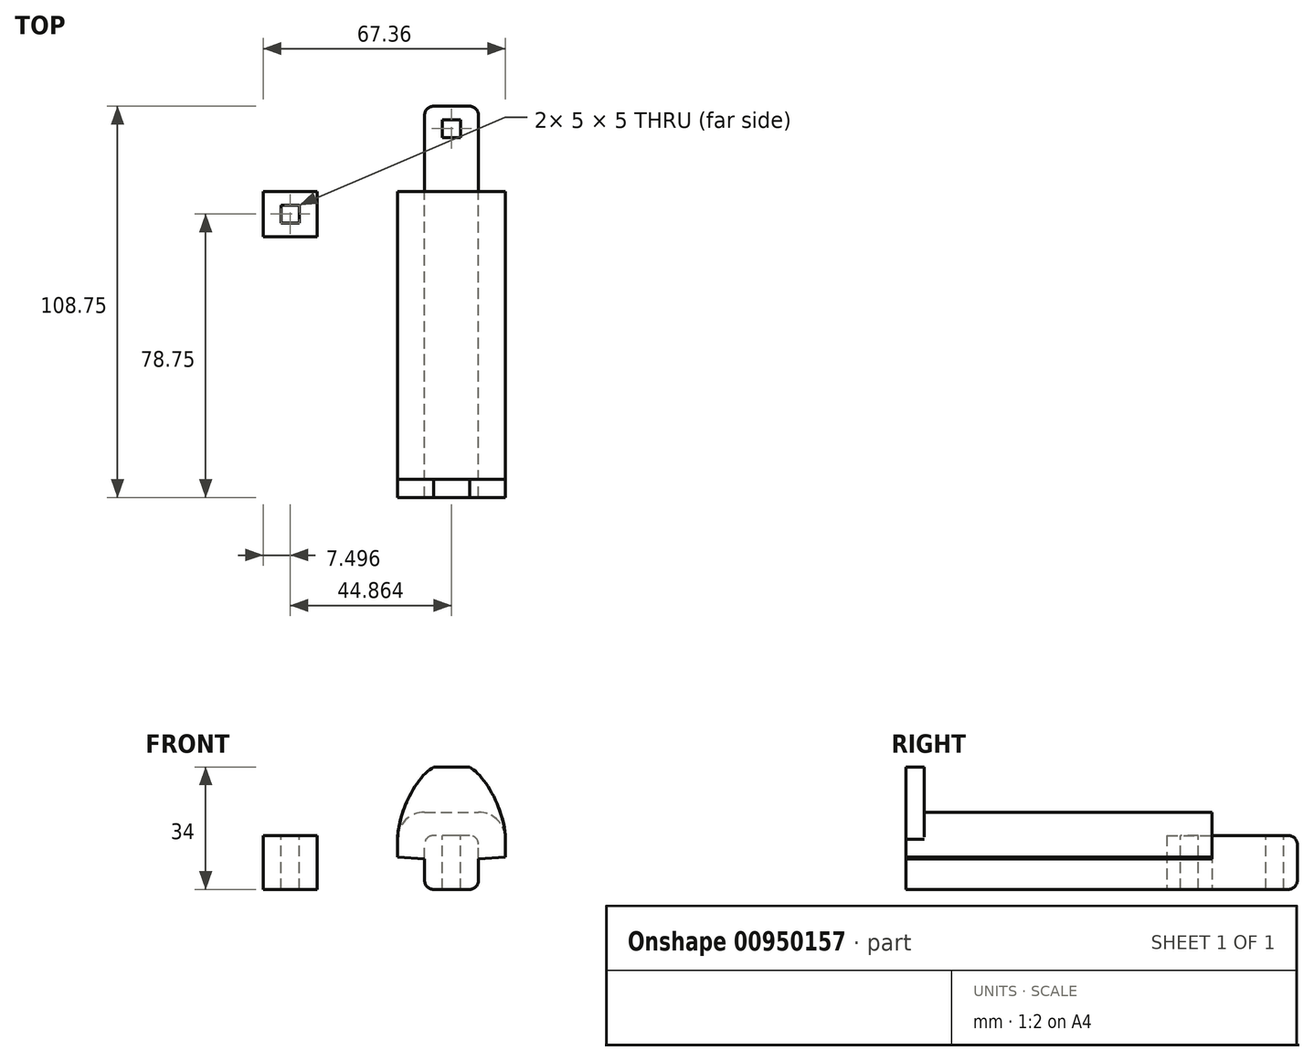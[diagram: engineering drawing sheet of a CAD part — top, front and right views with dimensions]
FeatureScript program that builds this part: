
annotation { "Feature Type Name" : "Feature", "Feature Type Description" : "" }
export const myFeature = defineFeature(function(context is Context, id is Id, definition is map)
    precondition{}
    {
        {
            var Q0;
            Q0=qCreatedBy(makeId("Front.planeOp"),FACE);
            var sketch = newSketch(context, id + "F0", { "sketchPlane" : qUnion([Q0])});
            skLineSegment(sketch, "E0.top", {"start": v(-5, -7.5) * mm, "end": v(5, -7.5) * mm});
            skPoint(sketch, "E0.middle", {"position": v(0, 0) * mm});
            skLineSegment(sketch, "E1", {"start": v(-15, 1.5) * mm, "end": v(-15, 6.5) * mm});
            skLineSegment(sketch, "E2.MirrorCS", {"start": v(15, 1.5) * mm, "end": v(15, 6.5) * mm});
            skPoint(sketch, "E3", {"position": v(7.5, 1) * mm});
            skLineSegment(sketch, "E4", {"start": v(-7.5, -5) * mm, "end": v(-7.5, 1) * mm});
            skLineSegment(sketch, "E5", {"start": v(7.5, -5) * mm, "end": v(7.5, 1) * mm});
            skLineSegment(sketch, "E6", {"start": v(-7.5, 14) * mm, "end": v(7.5, 14) * mm});
            skLineSegment(sketch, "E7", {"start": v(-7.5, 1) * mm, "end": v(-15, 1.5) * mm});
            skLineSegment(sketch, "E8", {"start": v(7.5, 1) * mm, "end": v(15, 1.5) * mm});
            skPoint(sketch, "E9.visualSharp", {"position": v(-15, 14) * mm});
            skArc(sketch, "E9.filletArc", {"start": v(-7.5, 14) * mm, "mid": v(-12.8, 11.8) * mm, "end": v(-15, 6.5) * mm});
            skPoint(sketch, "E10.visualSharp", {"position": v(15, 14) * mm});
            skArc(sketch, "E10.filletArc", {"start": v(15, 6.5) * mm, "mid": v(12.8, 11.8) * mm, "end": v(7.5, 14) * mm});
            skPoint(sketch, "E11.visualSharp", {"position": v(-7.5, -7.5) * mm});
            skArc(sketch, "E11.filletArc", {"start": v(-7.5, -5) * mm, "mid": v(-6.77, -6.77) * mm, "end": v(-5, -7.5) * mm});
            skPoint(sketch, "E12.visualSharp", {"position": v(7.5, -7.5) * mm});
            skArc(sketch, "E12.filletArc", {"start": v(5, -7.5) * mm, "mid": v(6.77, -6.77) * mm, "end": v(7.5, -5) * mm});
            skSolve(sketch);
        }
        {
            var Q0;
            Q0 = qSketchRegion(id + "F0", true);
            extrude(context, id + "F1", {"entities" : qUnion([Q0]), "depth" : 80 * mm, "offsetDistance" : 25 * mm});
        }
        {
            var Q0;
            Q0=makeQuery(id+"F1.opExtrude","CAP_FACE",FACE,{"disambiguationData":[OSD([sQuery(id+"F0.wireOp",EDGE,"E0.top"),sQuery(id+"F0.wireOp",EDGE,"E1"),sQuery(id+"F0.wireOp",EDGE,"E2.MirrorCS"),sQuery(id+"F0.wireOp",EDGE,"E4"),sQuery(id+"F0.wireOp",EDGE,"E5"),sQuery(id+"F0.wireOp",EDGE,"E6"),sQuery(id+"F0.wireOp",EDGE,"E7"),sQuery(id+"F0.wireOp",EDGE,"E8"),sQuery(id+"F0.wireOp",EDGE,"E9.filletArc"),sQuery(id+"F0.wireOp",EDGE,"E10.filletArc"),sQuery(id+"F0.wireOp",EDGE,"E11.filletArc"),sQuery(id+"F0.wireOp",EDGE,"E12.filletArc")])],"isStart":true});
            var sketch = newSketch(context, id + "F2", { "sketchPlane" : qUnion([Q0])});
            skLineSegment(sketch, "E13.bottom", {"start": v(-5, -7.5) * mm, "end": v(5, -7.5) * mm});
            skLineSegment(sketch, "E13.top", {"start": v(-5, 7.5) * mm, "end": v(5, 7.5) * mm});
            skLineSegment(sketch, "E13.left", {"start": v(-7.5, -5) * mm, "end": v(-7.5, 5) * mm});
            skLineSegment(sketch, "E13.right", {"start": v(7.5, -5) * mm, "end": v(7.5, 5) * mm});
            skPoint(sketch, "E13.middle", {"position": v(0, 0) * mm});
            skPoint(sketch, "E14.visualSharp", {"position": v(-7.5, 7.5) * mm});
            skArc(sketch, "E14.filletArc", {"start": v(-5, 7.5) * mm, "mid": v(-6.77, 6.77) * mm, "end": v(-7.5, 5) * mm});
            skPoint(sketch, "E15.visualSharp", {"position": v(7.5, 7.5) * mm});
            skArc(sketch, "E15.filletArc", {"start": v(7.5, 5) * mm, "mid": v(6.77, 6.77) * mm, "end": v(5, 7.5) * mm});
            skPoint(sketch, "E16.visualSharp", {"position": v(7.5, -7.5) * mm});
            skArc(sketch, "E16.filletArc", {"start": v(5, -7.5) * mm, "mid": v(6.77, -6.77) * mm, "end": v(7.5, -5) * mm});
            skPoint(sketch, "E17.visualSharp", {"position": v(-7.5, -7.5) * mm});
            skArc(sketch, "E17.filletArc", {"start": v(-7.5, -5) * mm, "mid": v(-6.77, -6.77) * mm, "end": v(-5, -7.5) * mm});
            skSolve(sketch);
        }
        {
            var Q0;
            Q0=makeQuery(id+"F2.imprint","IMPRINT",FACE,{"disambiguationData":[TD([[makeQuery(id+"F2.imprint","IMPRINT",EDGE,{"derivedFrom":sQuery(id+"F2.wireOp",EDGE,"E13.bottom")}),-1.0]])]});
            extrude(context, id + "F3", {"entities" : qUnion([Q0]), "operationType" : NewBodyOperationType.ADD, "depth" : 23.75 * mm, "offsetDistance" : 25 * mm});
        }
        {
            var Q0;
            Q0=makeQuery(id+"F3.opExtrude","SWEPT_FACE",FACE,{"disambiguationData":[OSD([sQuery(id+"F2.wireOp",EDGE,"E13.top")])]});
            var sketch = newSketch(context, id + "F4", { "sketchPlane" : qUnion([Q0])});
            skLineSegment(sketch, "E18.bottom", {"start": v(2.5, 20) * mm, "end": v(-2.5, 20) * mm});
            skLineSegment(sketch, "E18.top", {"start": v(2.5, 15) * mm, "end": v(-2.5, 15) * mm});
            skLineSegment(sketch, "E18.left", {"start": v(2.5, 20) * mm, "end": v(2.5, 15) * mm});
            skLineSegment(sketch, "E18.right", {"start": v(-2.5, 20) * mm, "end": v(-2.5, 15) * mm});
            skPoint(sketch, "E18.middle", {"position": v(0, 17.5) * mm});
            skSolve(sketch);
        }
        {
            var Q0;
            Q0=makeQuery(id+"F4.imprint","IMPRINT",FACE,{"disambiguationData":[TD([[makeQuery(id+"F4.imprint","IMPRINT",EDGE,{"derivedFrom":sQuery(id+"F4.wireOp",EDGE,"E18.bottom")}),1.0]])]});
            extrude(context, id + "F5", {"entities" : qUnion([Q0]), "operationType" : NewBodyOperationType.REMOVE, "oppositeDirection" : true, "depth" : 15 * mm, "offsetDistance" : 25 * mm});
        }
        {
            var Q0;
            Q0=makeQuery(id+"F1.opExtrude","CAP_FACE",FACE,{"disambiguationData":[OSD([sQuery(id+"F0.wireOp",EDGE,"E0.top"),sQuery(id+"F0.wireOp",EDGE,"E1"),sQuery(id+"F0.wireOp",EDGE,"E2.MirrorCS"),sQuery(id+"F0.wireOp",EDGE,"E4"),sQuery(id+"F0.wireOp",EDGE,"E5"),sQuery(id+"F0.wireOp",EDGE,"E6"),sQuery(id+"F0.wireOp",EDGE,"E7"),sQuery(id+"F0.wireOp",EDGE,"E8"),sQuery(id+"F0.wireOp",EDGE,"E9.filletArc"),sQuery(id+"F0.wireOp",EDGE,"E10.filletArc"),sQuery(id+"F0.wireOp",EDGE,"E11.filletArc"),sQuery(id+"F0.wireOp",EDGE,"E12.filletArc")])],"isStart":false});
            var sketch = newSketch(context, id + "F6", { "sketchPlane" : qUnion([Q0])});
            skLineSegment(sketch, "E19.top", {"start": v(-5, 26.5) * mm, "end": v(5, 26.5) * mm});
            skFitSpline(sketch, "E20", {"points": [v(-5, 26.5) * mm, v(-15, 6.5) * mm], "startDerivative": vector(-12.32, -6.2) * mm, "endDerivative": vector(-0.54, -24.82) * mm});
            skFitSpline(sketch, "E21.MirrorCS", {"points": [v(5, 26.5) * mm, v(15, 6.5) * mm], "startDerivative": vector(12.32, -6.2) * mm, "endDerivative": vector(0.54, -24.82) * mm});
            skSolve(sketch);
        }
        {
            var Q0;
            Q0=makeQuery(id+"F6.imprint","IMPRINT",FACE,{"disambiguationData":[TD([[makeQuery(id+"F6.imprint","IMPRINT",EDGE,{"derivedFrom":makeQuery(id+"F1.opExtrude","CAP_EDGE",EDGE,{"disambiguationData":[OSD([sQuery(id+"F0.wireOp",EDGE,"E0.top")])],"isStart":false})}),1.0]])]});
            var Q1;
            {var subQ1=sQuery(id+"F6.wireOp",EDGE,"E19.top");Q1=makeQuery(id+"F6.imprint","IMPRINT",FACE,{"disambiguationData":[TD([[makeQuery(id+"F6.imprint","IMPRINT",EDGE,{"derivedFrom":subQ1}),-1.0]])]});}
            extrude(context, id + "F7", {"entities" : qUnion([Q0, Q1]), "operationType" : NewBodyOperationType.ADD, "depth" : 5 * mm, "offsetDistance" : 25 * mm});
        }
        {
            var Q0;
            Q0=qCreatedBy(makeId("Front.planeOp"),FACE);
            var sketch = newSketch(context, id + "F8", { "sketchPlane" : qUnion([Q0])});
            skLineSegment(sketch, "E22.bottom", {"start": v(-52.36, 7.5) * mm, "end": v(-37.36, 7.5) * mm});
            skLineSegment(sketch, "E22.top", {"start": v(-52.36, -7.5) * mm, "end": v(-37.36, -7.5) * mm});
            skLineSegment(sketch, "E22.left", {"start": v(-52.36, 7.5) * mm, "end": v(-52.36, -7.5) * mm});
            skLineSegment(sketch, "E22.right", {"start": v(-37.36, 7.5) * mm, "end": v(-37.36, -7.5) * mm});
            skPoint(sketch, "E22.middle", {"position": v(-44.86, 0) * mm});
            skSolve(sketch);
        }
        {
            var Q0;
            Q0=makeQuery(id+"F8.imprint","IMPRINT",FACE,{"disambiguationData":[TD([[makeQuery(id+"F8.imprint","IMPRINT",EDGE,{"derivedFrom":sQuery(id+"F8.wireOp",EDGE,"E22.bottom")}),-1.0]])]});
            extrude(context, id + "F9", {"entities" : qUnion([Q0]), "depth" : 12.5 * mm, "offsetDistance" : 25 * mm});
        }
        {
            var Q0;
            Q0=makeQuery(id+"F9.opExtrude","SWEPT_FACE",FACE,{"disambiguationData":[OSD([sQuery(id+"F8.wireOp",EDGE,"E22.bottom")])]});
            var sketch = newSketch(context, id + "F10", { "sketchPlane" : qUnion([Q0])});
            skLineSegment(sketch, "E23.bottom", {"start": v(-47.36, -3.75) * mm, "end": v(-42.36, -3.75) * mm});
            skLineSegment(sketch, "E23.top", {"start": v(-47.36, -8.75) * mm, "end": v(-42.36, -8.75) * mm});
            skLineSegment(sketch, "E23.left", {"start": v(-47.36, -3.75) * mm, "end": v(-47.36, -8.75) * mm});
            skLineSegment(sketch, "E23.right", {"start": v(-42.36, -3.75) * mm, "end": v(-42.36, -8.75) * mm});
            skSolve(sketch);
        }
        {
            var Q0;
            Q0=makeQuery(id+"F10.imprint","IMPRINT",FACE,{"disambiguationData":[TD([[makeQuery(id+"F10.imprint","IMPRINT",EDGE,{"derivedFrom":sQuery(id+"F10.wireOp",EDGE,"E23.bottom")}),-1.0]])]});
            extrude(context, id + "F11", {"entities" : qUnion([Q0]), "operationType" : NewBodyOperationType.REMOVE, "oppositeDirection" : true, "depth" : 15 * mm, "offsetDistance" : 25 * mm});
        }
        {
            var Q0;
            Q0=makeQuery(id+"F3.opExtrude","CAP_EDGE",EDGE,{"disambiguationData":[OSD([sQuery(id+"F2.wireOp",EDGE,"E13.top")])],"isStart":false});
            var Q1;
            Q1=makeQuery(id+"F3.opExtrude","CAP_EDGE",EDGE,{"disambiguationData":[OSD([sQuery(id+"F2.wireOp",EDGE,"E13.left")])],"isStart":false});
            fillet(context, id + "F12", {"entities" : qUnion([Q0, Q1]), "radius" : 2.5 * mm, "tangentPropagation" : true, "allowEdgeOverflow" : false});
        }
    });
